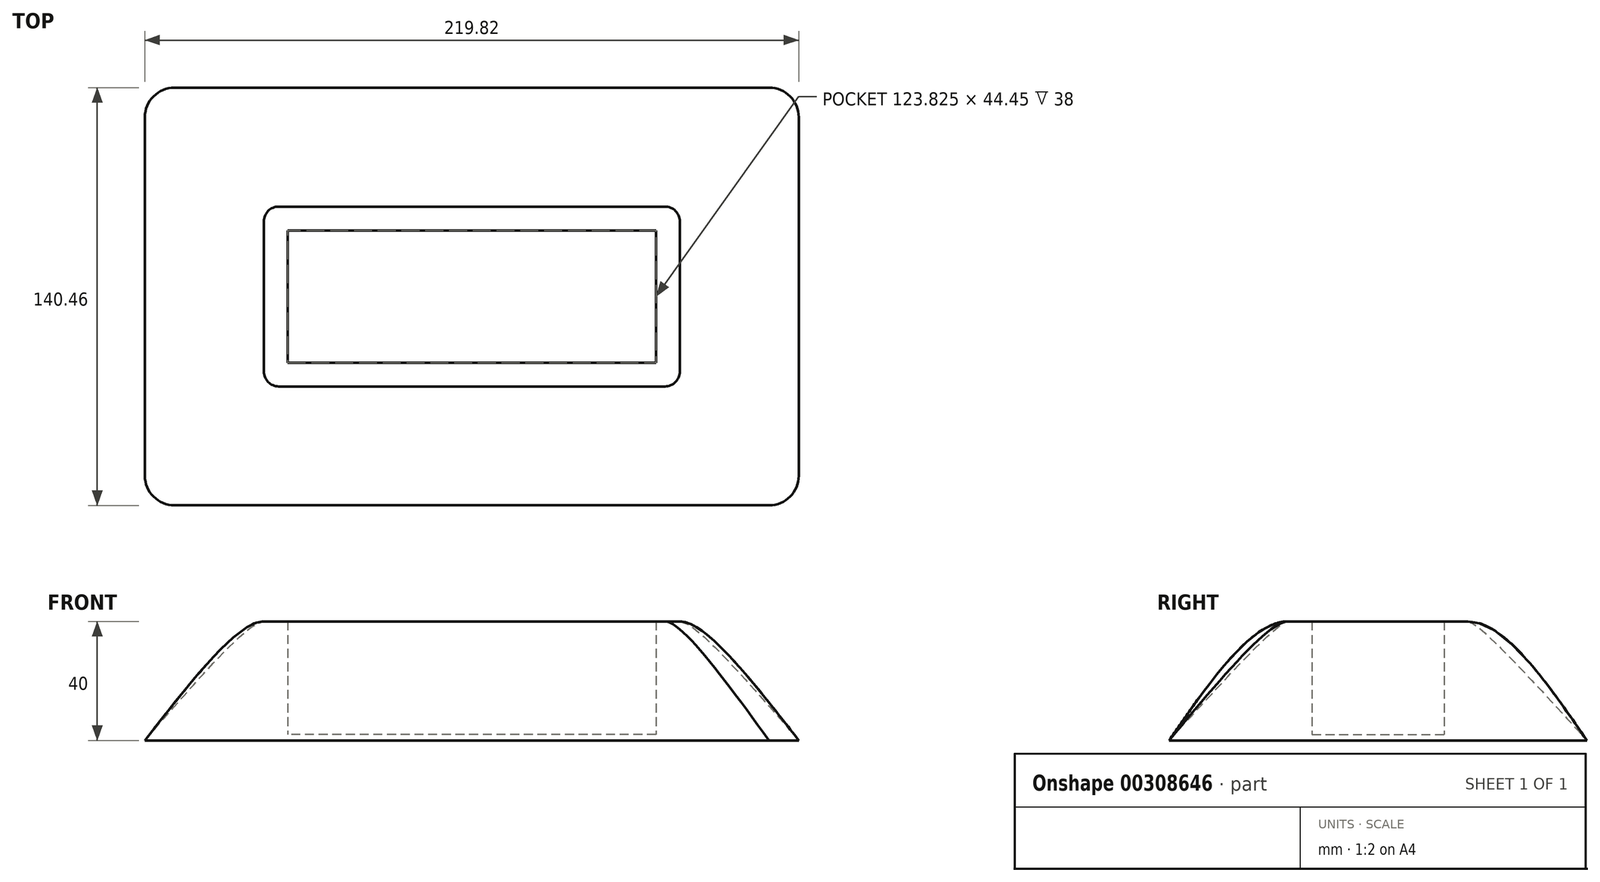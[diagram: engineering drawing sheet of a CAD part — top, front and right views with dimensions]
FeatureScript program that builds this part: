
annotation { "Feature Type Name" : "Feature", "Feature Type Description" : "" }
export const myFeature = defineFeature(function(context is Context, id is Id, definition is map)
    precondition{}
    {
        {
            assignVariable(context, id + "F0", {"name" : "height", "anyValue" : 40});
        }
        {
            var Q0;
            Q0=qCreatedBy(makeId("Top.planeOp"),FACE);
            var sketch = newSketch(context, id + "F1", { "sketchPlane" : qUnion([Q0])});
            skLineSegment(sketch, "E0.bottom", {"start": v(61.91, -22.23) * mm, "end": v(-61.91, -22.23) * mm});
            skLineSegment(sketch, "E0.top", {"start": v(61.91, 22.23) * mm, "end": v(-61.91, 22.23) * mm});
            skLineSegment(sketch, "E0.left", {"start": v(61.91, -22.23) * mm, "end": v(61.91, 22.23) * mm});
            skLineSegment(sketch, "E0.right", {"start": v(-61.91, -22.23) * mm, "end": v(-61.91, 22.22) * mm});
            skPoint(sketch, "E0.middle", {"position": v(0, 0) * mm});
            skLineSegment(sketch, "E1.0", {"start": v(64.91, 30.23) * mm, "end": v(-64.91, 30.23) * mm});
            skLineSegment(sketch, "E1.1", {"start": v(69.91, -25.23) * mm, "end": v(69.91, 25.22) * mm});
            skLineSegment(sketch, "E1.2", {"start": v(64.91, -30.23) * mm, "end": v(-64.91, -30.23) * mm});
            skLineSegment(sketch, "E1.3", {"start": v(-69.91, -25.23) * mm, "end": v(-69.91, 25.23) * mm});
            skLineSegment(sketch, "E2.0", {"start": v(99.91, 70.22) * mm, "end": v(-99.91, 70.22) * mm});
            skLineSegment(sketch, "E2.1", {"start": v(109.91, -60.22) * mm, "end": v(109.91, 60.23) * mm});
            skLineSegment(sketch, "E2.2", {"start": v(99.91, -70.22) * mm, "end": v(-99.91, -70.23) * mm});
            skLineSegment(sketch, "E2.3", {"start": v(-109.91, -60.23) * mm, "end": v(-109.91, 60.22) * mm});
            skPoint(sketch, "E3.visualSharp", {"position": v(-109.91, 70.22) * mm});
            skArc(sketch, "E3.filletArc", {"start": v(-99.91, 70.22) * mm, "mid": v(-106.98, 67.3) * mm, "end": v(-109.91, 60.22) * mm});
            skPoint(sketch, "E4.visualSharp", {"position": v(109.91, 70.22) * mm});
            skArc(sketch, "E4.filletArc", {"start": v(109.91, 60.23) * mm, "mid": v(106.98, 67.3) * mm, "end": v(99.91, 70.22) * mm});
            skPoint(sketch, "E5.visualSharp", {"position": v(109.91, -70.22) * mm});
            skArc(sketch, "E5.filletArc", {"start": v(99.91, -70.22) * mm, "mid": v(106.98, -67.3) * mm, "end": v(109.91, -60.22) * mm});
            skPoint(sketch, "E6.visualSharp", {"position": v(-109.91, -70.23) * mm});
            skArc(sketch, "E6.filletArc", {"start": v(-109.91, -60.23) * mm, "mid": v(-106.98, -67.3) * mm, "end": v(-99.91, -70.23) * mm});
            skPoint(sketch, "E7.visualSharp", {"position": v(-69.91, 30.23) * mm});
            skArc(sketch, "E7.filletArc", {"start": v(-64.91, 30.23) * mm, "mid": v(-68.45, 28.76) * mm, "end": v(-69.91, 25.23) * mm});
            skPoint(sketch, "E8.visualSharp", {"position": v(69.91, 30.23) * mm});
            skArc(sketch, "E8.filletArc", {"start": v(69.91, 25.22) * mm, "mid": v(68.45, 28.76) * mm, "end": v(64.91, 30.23) * mm});
            skPoint(sketch, "E9.visualSharp", {"position": v(69.91, -30.23) * mm});
            skArc(sketch, "E9.filletArc", {"start": v(64.91, -30.23) * mm, "mid": v(68.45, -28.76) * mm, "end": v(69.91, -25.23) * mm});
            skPoint(sketch, "E10.visualSharp", {"position": v(-69.91, -30.23) * mm});
            skArc(sketch, "E10.filletArc", {"start": v(-69.91, -25.23) * mm, "mid": v(-68.45, -28.76) * mm, "end": v(-64.91, -30.23) * mm});
            skSolve(sketch);
        }
        {
            var Q0;
            Q0=qCreatedBy(makeId("Top.planeOp"),FACE);
            cPlane(context, id + "F2", {"entities" : qUnion([Q0]), "cplaneType" : CPlaneType.OFFSET, "offset" : getVariable(context, 'height') * mm, "width" : 150 * mm, "height" : 150 * mm});
        }
        {
            var Q0;
            Q0=qCreatedBy(id+"F2.planeOp",FACE);
            var sketch = newSketch(context, id + "F3", { "sketchPlane" : qUnion([Q0])});
            skArc(sketch, "E11.0", {"start": v(69.91, 25.22) * mm, "mid": v(68.45, 28.76) * mm, "end": v(64.91, 30.23) * mm});
            skLineSegment(sketch, "E11.1", {"start": v(69.91, -25.23) * mm, "end": v(69.91, 25.22) * mm});
            skLineSegment(sketch, "E11.2", {"start": v(64.91, 30.23) * mm, "end": v(-64.91, 30.23) * mm});
            skArc(sketch, "E11.3", {"start": v(64.91, -30.23) * mm, "mid": v(68.45, -28.76) * mm, "end": v(69.91, -25.23) * mm});
            skArc(sketch, "E11.4", {"start": v(-69.91, -25.23) * mm, "mid": v(-68.45, -28.76) * mm, "end": v(-64.91, -30.23) * mm});
            skArc(sketch, "E11.5", {"start": v(-64.91, 30.23) * mm, "mid": v(-68.45, 28.76) * mm, "end": v(-69.91, 25.23) * mm});
            skLineSegment(sketch, "E11.6", {"start": v(-69.91, -25.23) * mm, "end": v(-69.91, 25.23) * mm});
            skLineSegment(sketch, "E11.7", {"start": v(64.91, -30.23) * mm, "end": v(-64.91, -30.23) * mm});
            skSolve(sketch);
        }
        {
            var Q0;
            Q0=qCreatedBy(makeId("Top.planeOp"),FACE);
            var sketch = newSketch(context, id + "F4", { "sketchPlane" : qUnion([Q0])});
            skLineSegment(sketch, "E12.0.0", {"start": v(-99.91, -70.23) * mm, "end": v(99.91, -70.22) * mm});
            skArc(sketch, "E12.0.1", {"start": v(99.91, -70.22) * mm, "mid": v(106.98, -67.3) * mm, "end": v(109.91, -60.22) * mm});
            skLineSegment(sketch, "E12.0.2", {"start": v(109.91, -60.22) * mm, "end": v(109.91, 60.23) * mm});
            skArc(sketch, "E12.0.3", {"start": v(109.91, 60.23) * mm, "mid": v(106.98, 67.3) * mm, "end": v(99.91, 70.22) * mm});
            skLineSegment(sketch, "E12.0.4", {"start": v(99.91, 70.22) * mm, "end": v(-99.91, 70.22) * mm});
            skArc(sketch, "E12.0.5", {"start": v(-99.91, 70.22) * mm, "mid": v(-106.98, 67.3) * mm, "end": v(-109.91, 60.22) * mm});
            skLineSegment(sketch, "E12.0.6", {"start": v(-109.91, 60.22) * mm, "end": v(-109.91, -60.23) * mm});
            skArc(sketch, "E12.0.7", {"start": v(-109.91, -60.23) * mm, "mid": v(-106.98, -67.3) * mm, "end": v(-99.91, -70.23) * mm});
            skSolve(sketch);
        }
        {
            var Q0;
            Q0=makeQuery(id+"F4.imprint","IMPRINT",FACE,{"disambiguationData":[TD([[makeQuery(id+"F4.imprint","IMPRINT",EDGE,{"derivedFrom":sQuery(id+"F4.wireOp",EDGE,"E12.0.0")}),1.0]])]});
            var Q1;
            Q1=makeQuery(id+"F3.imprint","IMPRINT",FACE,{"disambiguationData":[TD([[makeQuery(id+"F3.imprint","IMPRINT",EDGE,{"derivedFrom":sQuery(id+"F3.wireOp",EDGE,"E11.0")}),1.0]])]});
            var Q2;
            Q2=sQuery(id+"F4.wireOp",VERTEX,"E12.0.0.end");
            var Q3;
            Q3=sQuery(id+"F3.wireOp",VERTEX,"E11.3.start");
            loft(context, id + "F5", {"endCondition" : LoftEndDerivativeType.TANGENT_TO_PROFILE, "endMagnitude" : .5, "sheetProfilesArray" : [{ "sheetProfileEntities" : qUnion([Q0]) }, { "sheetProfileEntities" : qUnion([Q1]) }], "matchConnections" : true, "connections" : [{ "connectionEntities" : qUnion([Q2, Q3]), "connectionEdgeQueries" : qUnion([]), "connectionEdgeParameters" : [] }]});
        }
        {
            var Q0;
            Q0=makeQuery(id+"F1.imprint","IMPRINT",FACE,{"disambiguationData":[TD([[makeQuery(id+"F1.imprint","IMPRINT",EDGE,{"derivedFrom":sQuery(id+"F1.wireOp",EDGE,"E0.bottom")}),-1.0]])]});
            var Q1;
            Q1=makeQuery(id+"F5.opLoft","CAP_FACE",FACE,{"disambiguationData":[OSD([makeQuery(id+"F3.imprint","IMPRINT",FACE,{"disambiguationData":[TD([[makeQuery(id+"F3.imprint","IMPRINT",EDGE,{"derivedFrom":sQuery(id+"F3.wireOp",EDGE,"E11.0")}),1.0]])]})])],"isStart":true});
            extrude(context, id + "F6", {"entities" : qUnion([Q0]), "operationType" : NewBodyOperationType.REMOVE, "endBound" : BoundingType.UP_TO_SURFACE, "endBoundEntityFace" : qUnion([Q1]), "depth" : 25 * mm, "hasSecondDirection" : true, "secondDirectionOppositeDirection" : false, "secondDirectionDepth" : 2 * mm});
        }
    });
